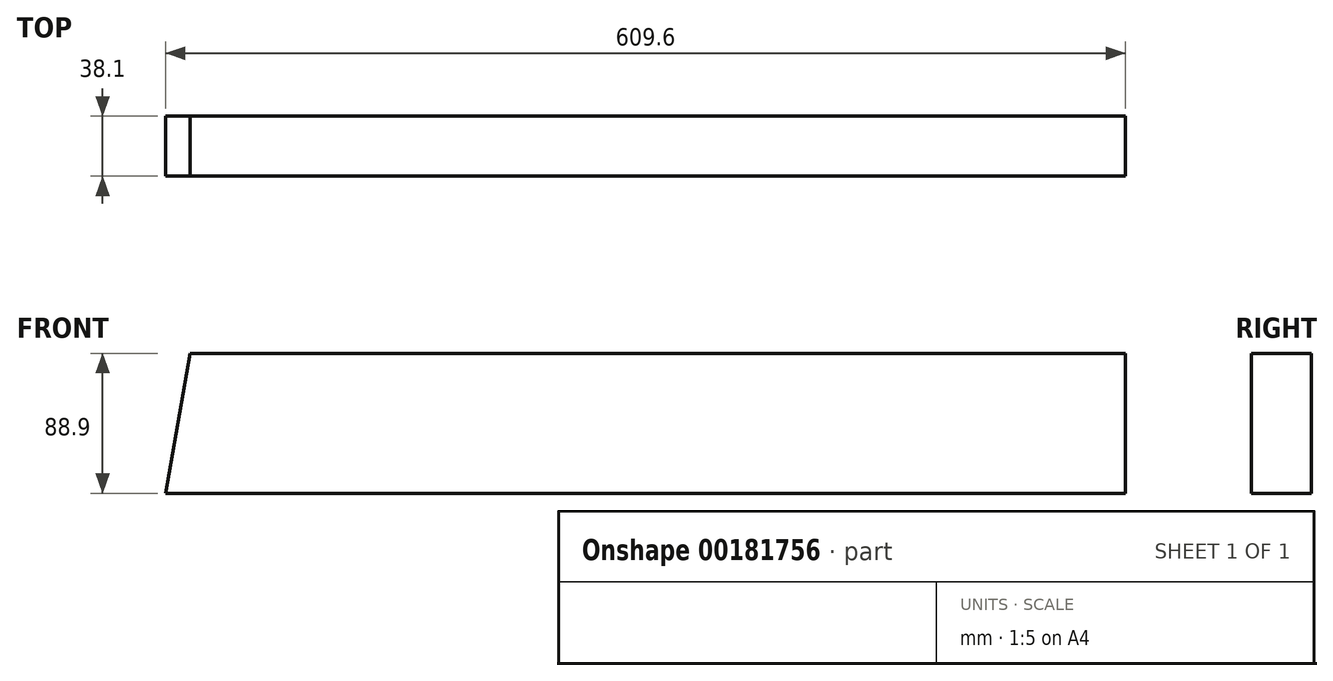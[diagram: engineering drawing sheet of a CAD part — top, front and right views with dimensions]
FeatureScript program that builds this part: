
annotation { "Feature Type Name" : "Feature", "Feature Type Description" : "" }
export const myFeature = defineFeature(function(context is Context, id is Id, definition is map)
    precondition{}
    {
        {
            var Q0;
            Q0=qCreatedBy(makeId("Front.planeOp"),FACE);
            var sketch = newSketch(context, id + "F0", { "sketchPlane" : qUnion([Q0])});
            skLineSegment(sketch, "E0.bottom", {"start": v(-145.35, 0) * mm, "end": v(464.25, 0) * mm});
            skLineSegment(sketch, "E0.top", {"start": v(-129.67, 88.9) * mm, "end": v(464.25, 88.9) * mm});
            skLineSegment(sketch, "E0.right", {"start": v(464.25, 0) * mm, "end": v(464.25, 88.9) * mm});
            skLineSegment(sketch, "E1", {"start": v(-129.67, 88.9) * mm, "end": v(-145.35, 0) * mm});
            skSolve(sketch);
        }
        {
            var Q0;
            Q0 = qSketchRegion(id + "F0", true);
            extrude(context, id + "F1", {"entities" : qUnion([Q0]), "depth" : 38.1 * mm});
        }
    });
